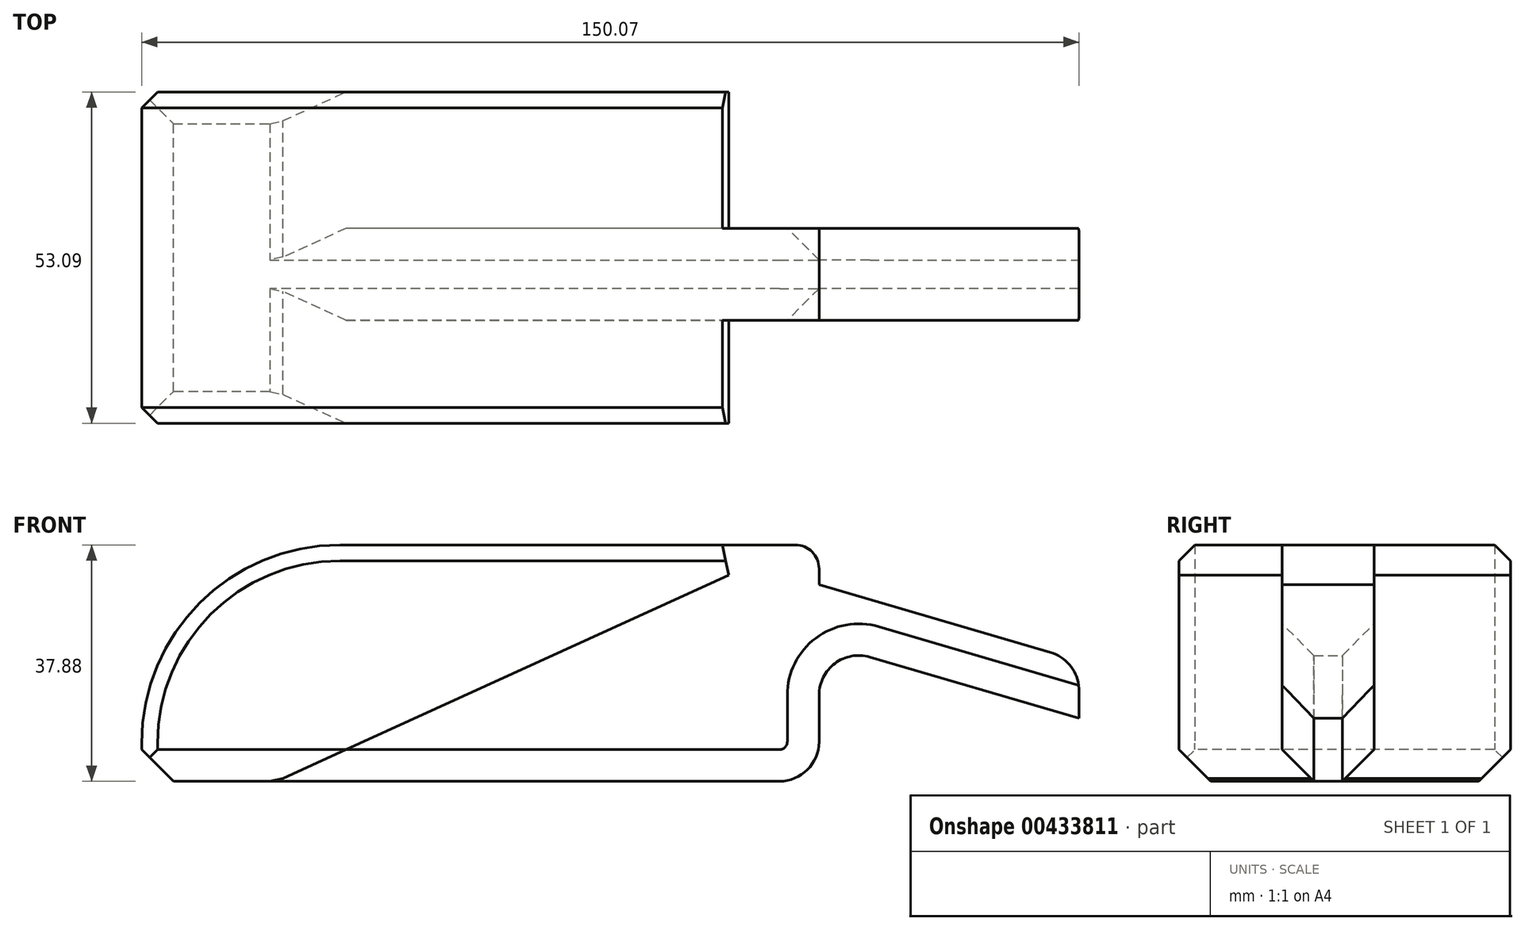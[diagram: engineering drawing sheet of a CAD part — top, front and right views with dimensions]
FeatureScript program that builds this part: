
annotation { "Feature Type Name" : "Feature", "Feature Type Description" : "" }
export const myFeature = defineFeature(function(context is Context, id is Id, definition is map)
    precondition{}
    {
        {
            var Q0;
            Q0=qCreatedBy(makeId("Front.planeOp"),FACE);
            var sketch = newSketch(context, id + "F0", { "sketchPlane" : qUnion([Q0])});
            skLineSegment(sketch, "E0", {"start": v(-139.07, -52.6) * mm, "end": v(-139.07, -46.48) * mm});
            skLineSegment(sketch, "E1", {"start": v(-107.32, -14.73) * mm, "end": v(-34.42, -14.73) * mm});
            skLineSegment(sketch, "E2", {"start": v(-30.61, -18.54) * mm, "end": v(-30.61, -21.1) * mm});
            skLineSegment(sketch, "E3", {"start": v(-30.61, -21.1) * mm, "end": v(6.43, -31.95) * mm});
            skLineSegment(sketch, "E4", {"start": v(11, -38.05) * mm, "end": v(11, -42.5) * mm});
            skLineSegment(sketch, "E5", {"start": v(11, -42.5) * mm, "end": v(-22.48, -32.7) * mm});
            skLineSegment(sketch, "E6", {"start": v(-30.61, -38.8) * mm, "end": v(-30.61, -46.26) * mm});
            skLineSegment(sketch, "E7", {"start": v(-36.96, -52.6) * mm, "end": v(-139.07, -52.6) * mm});
            skPoint(sketch, "E8.visualSharp", {"position": v(-30.61, -14.73) * mm});
            skArc(sketch, "E8.filletArc", {"start": v(-30.61, -18.54) * mm, "mid": v(-31.73, -15.84) * mm, "end": v(-34.42, -14.73) * mm});
            skPoint(sketch, "E9.visualSharp", {"position": v(-30.61, -52.6) * mm});
            skArc(sketch, "E9.filletArc", {"start": v(-36.96, -52.6) * mm, "mid": v(-32.47, -50.75) * mm, "end": v(-30.61, -46.26) * mm});
            skPoint(sketch, "E10.visualSharp", {"position": v(-30.61, -30.32) * mm});
            skArc(sketch, "E10.filletArc", {"start": v(-22.48, -32.7) * mm, "mid": v(-28.07, -33.71) * mm, "end": v(-30.61, -38.8) * mm});
            skPoint(sketch, "E11.visualSharp", {"position": v(11, -33.29) * mm});
            skArc(sketch, "E11.filletArc", {"start": v(11, -38.05) * mm, "mid": v(9.73, -34.24) * mm, "end": v(6.43, -31.95) * mm});
            skPoint(sketch, "E12.visualSharp", {"position": v(-139.07, -14.73) * mm});
            skArc(sketch, "E12.filletArc", {"start": v(-107.32, -14.73) * mm, "mid": v(-129.77, -24.03) * mm, "end": v(-139.07, -46.48) * mm});
            skLineSegment(sketch, "E13", {"start": v(-34.42, -14.73) * mm, "end": v(-117.44, -52.6) * mm});
            skSolve(sketch);
        }
        {
            var Q0;
            {var subQ1=sQuery(id+"F0.wireOp",EDGE,"E0");Q0=makeQuery(id+"F0.imprint","IMPRINT",FACE,{"disambiguationData":[TD([[makeQuery(id+"F0.imprint","IMPRINT",EDGE,{"derivedFrom":subQ1}),-1.0]])]});}
            extrude(context, id + "F1", {"entities" : qUnion([Q0]), "depth" : 22.6 * mm, "hasSecondDirection" : true, "secondDirectionOppositeDirection" : true, "secondDirectionDepth" : 30.48 * mm});
        }
        {
            var Q0;
            Q0=makeQuery(id+"F0.imprint","IMPRINT",FACE,{"disambiguationData":[TD([[makeQuery(id+"F0.imprint","IMPRINT",EDGE,{"derivedFrom":sQuery(id+"F0.wireOp",EDGE,"E2")}),-1.0]])]});
            extrude(context, id + "F2", {"entities" : qUnion([Q0]), "operationType" : NewBodyOperationType.ADD, "depth" : 6.1 * mm, "hasSecondDirection" : true, "secondDirectionOppositeDirection" : true, "secondDirectionDepth" : 8.64 * mm});
        }
        {
            var Q0;
            {var subQ0=sQuery(id+"F0.wireOp",EDGE,"E7");Q0=makeQuery(id+"F2.boolean.opBoolean","MERGE",FACE,{"derivedFrom":[makeQuery(id+"F1.opExtrude","SWEPT_FACE",FACE,{"disambiguationData":[OSD([subQ0])]}),makeQuery(id+"F2.opExtrude","SWEPT_FACE",FACE,{"disambiguationData":[OSD([subQ0])]})]});}
            chamfer(context, id + "F3", {"entities" : qUnion([Q0]), "width" : 5.08 * mm, "tangentPropagation" : true});
        }
        {
            var Q0;
            Q0=makeQuery(id+"F1.opExtrude","SWEPT_FACE",FACE,{"disambiguationData":[OSD([sQuery(id+"F0.wireOp",EDGE,"E1")])]});
            chamfer(context, id + "F4", {"entities" : qUnion([Q0]), "width" : 2.54 * mm, "tangentPropagation" : true});
        }
    });
